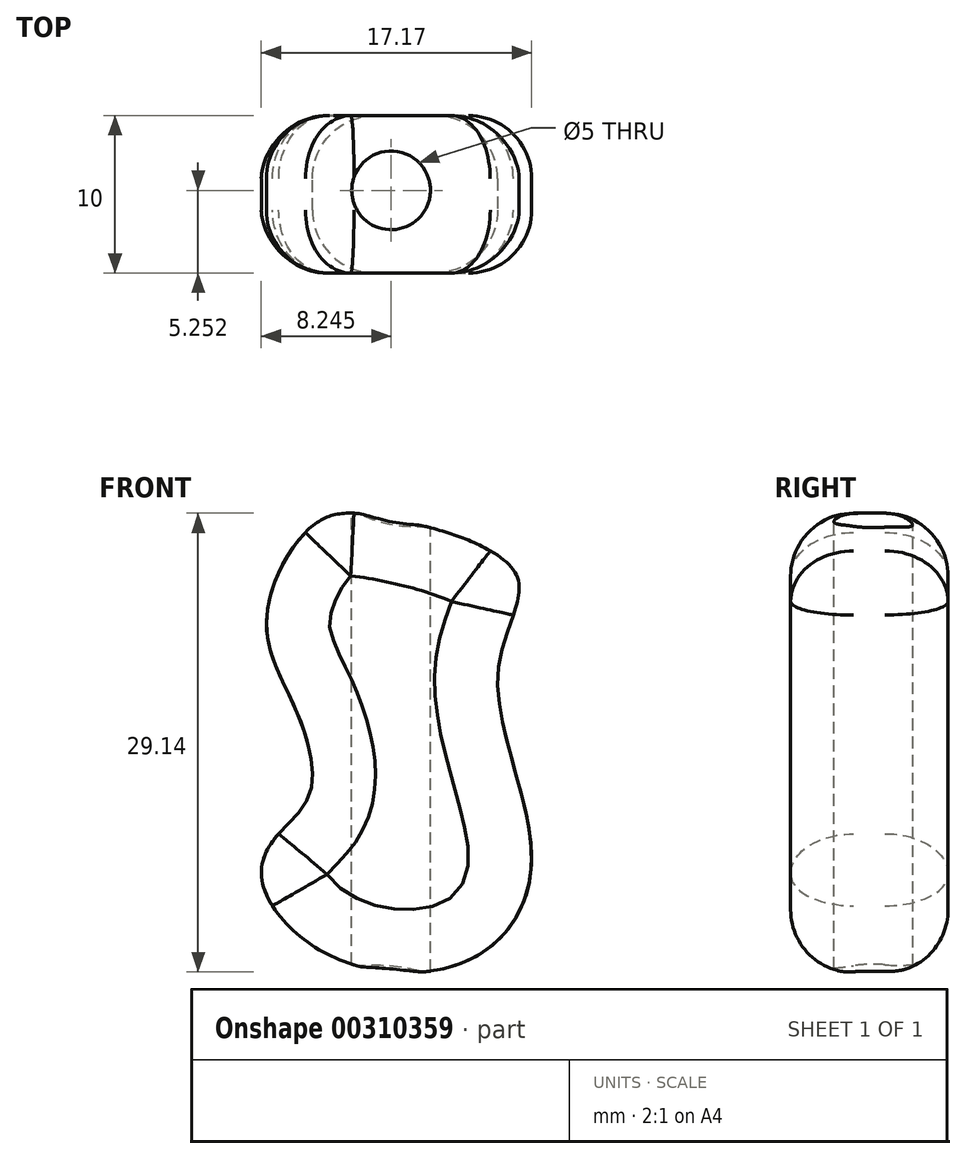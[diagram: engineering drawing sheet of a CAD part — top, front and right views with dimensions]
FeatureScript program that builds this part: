
annotation { "Feature Type Name" : "Feature", "Feature Type Description" : "" }
export const myFeature = defineFeature(function(context is Context, id is Id, definition is map)
    precondition{}
    {
        {
            var Q0;
            Q0=qCreatedBy(makeId("Front.planeOp"),FACE);
            var sketch = newSketch(context, id + "F0", { "sketchPlane" : qUnion([Q0])});
            skFitSpline(sketch, "E0", {"points": [v(1.67, 5.1) * mm, v(-2.7, 4.54) * mm, v(-5.65, -1.54) * mm, v(-3.65, -7.48) * mm, v(-2.9, -12.5) * mm, v(-4.77, -14.93) * mm, v(-5.96, -17.81) * mm, v(-1.77, -22.7) * mm, v(7.3, -23) * mm, v(11.19, -16.56) * mm, v(9.06, -4.6) * mm, v(10.19, 1.47) * mm, v(1.67, 5.1) * mm]});
            skSolve(sketch);
        }
        {
            var Q0;
            Q0=makeQuery(id+"F0.imprint","IMPRINT",FACE,{"disambiguationData":[TD([[makeQuery(id+"F0.imprint","IMPRINT",EDGE,{"derivedFrom":sQuery(id+"F0.wireOp",EDGE,"E0")}),1.0]])]});
            extrude(context, id + "F1", {"entities" : qUnion([Q0]), "depth" : 10 * mm});
        }
        {
            var Q0;
            Q0=makeQuery(id+"F1.opExtrude","CAP_EDGE",EDGE,{"disambiguationData":[OSD([sQuery(id+"F0.wireOp",EDGE,"E0")])],"isStart":false});
            var Q1;
            Q1=makeQuery(id+"F1.opExtrude","CAP_EDGE",EDGE,{"disambiguationData":[OSD([sQuery(id+"F0.wireOp",EDGE,"E0")])],"isStart":true});
            fillet(context, id + "F2", {"entities" : qUnion([Q0, Q1]), "radius" : 4 * mm, "tangentPropagation" : true, "allowEdgeOverflow" : false});
        }
        {
            var Q0;
            Q0=qCreatedBy(makeId("Top.planeOp"),FACE);
            var sketch = newSketch(context, id + "F3", { "sketchPlane" : qUnion([Q0])});
            skCircle(sketch, "E1", {"center": v(2.26, -4.75) * mm, "radius": 2.5 * mm});
            skSolve(sketch);
        }
        {
            var Q0;
            Q0 = qSketchRegion(id + "F3", true);
            var Q1;
            Q1=sQuery(id+"F3.wireOp",EDGE,"E1");
            extrude(context, id + "F4", {"entities" : qUnion([Q0]), "operationType" : NewBodyOperationType.REMOVE, "surfaceEntities" : qUnion([Q1]), "endBound" : BoundingType.SYMMETRIC, "oppositeDirection" : true, "depth" : 61.8 * mm});
        }
    });
